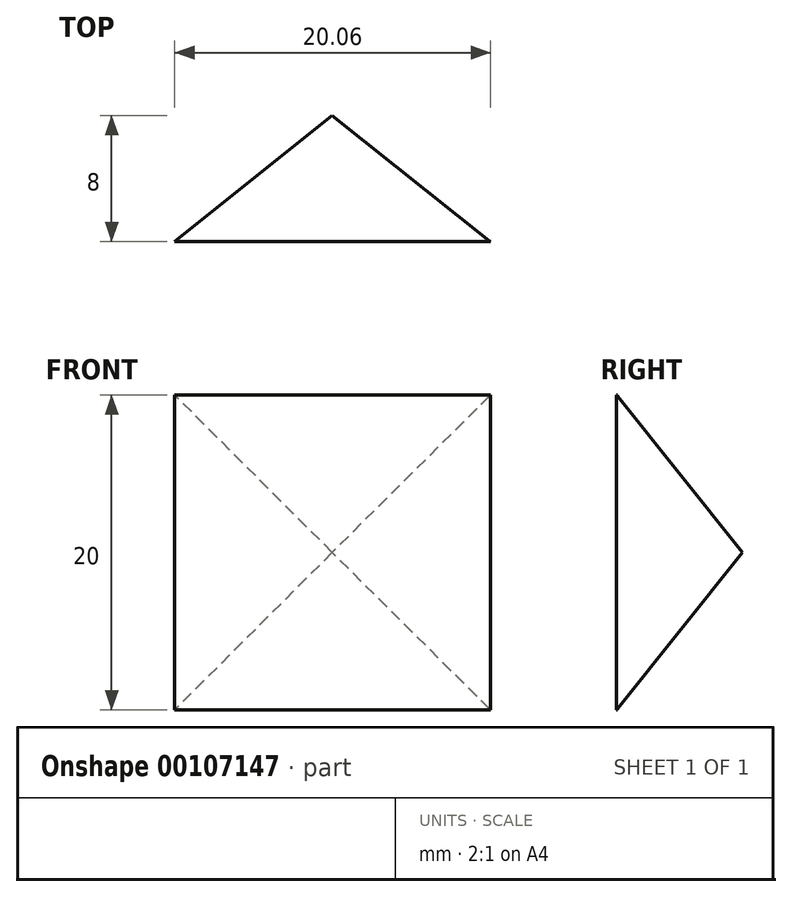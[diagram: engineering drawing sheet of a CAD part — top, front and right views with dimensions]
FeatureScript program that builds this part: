
annotation { "Feature Type Name" : "Feature", "Feature Type Description" : "" }
export const myFeature = defineFeature(function(context is Context, id is Id, definition is map)
    precondition{}
    {
        {
            var Q0;
            Q0=qCreatedBy(makeId("Front.planeOp"),FACE);
            var sketch = newSketch(context, id + "F0", { "sketchPlane" : qUnion([Q0])});
            skLineSegment(sketch, "E0.bottom", {"start": v(0, 0) * mm, "end": v(20, 0) * mm});
            skLineSegment(sketch, "E0.top", {"start": v(0, 20) * mm, "end": v(20, 20) * mm});
            skLineSegment(sketch, "E0.left", {"start": v(0, 0) * mm, "end": v(0, 20) * mm});
            skLineSegment(sketch, "E0.right", {"start": v(20, 0) * mm, "end": v(20, 20) * mm});
            skLineSegment(sketch, "E1", {"start": v(-5.03, 10) * mm, "end": v(28.52, 10) * mm, "construction": true});
            skLineSegment(sketch, "E2", {"start": v(10, 25.44) * mm, "end": v(10, -9.41) * mm, "construction": true});
            skSolve(sketch);
        }
        {
            var Q0;
            Q0=qCreatedBy(makeId("Top.planeOp"),FACE);
            var sketch = newSketch(context, id + "F1", { "sketchPlane" : qUnion([Q0])});
            skLineSegment(sketch, "E3", {"start": v(10, -17.71) * mm, "end": v(10, 8) * mm, "construction": true});
            skLineSegment(sketch, "E4", {"start": v(0, 0) * mm, "end": v(10, 8) * mm});
            skLineSegment(sketch, "E5", {"start": v(10, 8) * mm, "end": v(20.06, 0) * mm});
            skLineSegment(sketch, "E6", {"start": v(0, 0) * mm, "end": v(20.06, 0) * mm});
            skSolve(sketch);
        }
        {
            var Q0;
            Q0=makeQuery(id+"F1.imprint","IMPRINT",FACE,{"disambiguationData":[TD([[makeQuery(id+"F1.imprint","IMPRINT",EDGE,{"derivedFrom":sQuery(id+"F1.wireOp",EDGE,"E4")}),-1.0]])]});
            extrude(context, id + "F2", {"entities" : qUnion([Q0]), "depth" : 20 * mm});
        }
        {
            var Q0;
            Q0=qCreatedBy(makeId("Right.planeOp"),FACE);
            var sketch = newSketch(context, id + "F3", { "sketchPlane" : qUnion([Q0])});
            skLineSegment(sketch, "E7", {"start": v(-7.8, 10) * mm, "end": v(44.74, 10) * mm, "construction": true});
            skLineSegment(sketch, "E8", {"start": v(0, 0) * mm, "end": v(8, 0) * mm});
            skLineSegment(sketch, "E9", {"start": v(8, 0) * mm, "end": v(8, 10) * mm});
            skLineSegment(sketch, "E10", {"start": v(8, 10) * mm, "end": v(0, 0) * mm});
            skLineSegment(sketch, "E11.MirrorCS", {"start": v(8, 10) * mm, "end": v(0, 20) * mm});
            skLineSegment(sketch, "E12.MirrorCS", {"start": v(0, 20) * mm, "end": v(8, 20) * mm});
            skLineSegment(sketch, "E13.MirrorCS", {"start": v(8, 20) * mm, "end": v(8, 10) * mm});
            skSolve(sketch);
        }
        {
            var Q0;
            Q0 = qSketchRegion(id + "F3", true);
            extrude(context, id + "F4", {"entities" : qUnion([Q0]), "operationType" : NewBodyOperationType.REMOVE, "depth" : 20 * mm});
        }
    });
